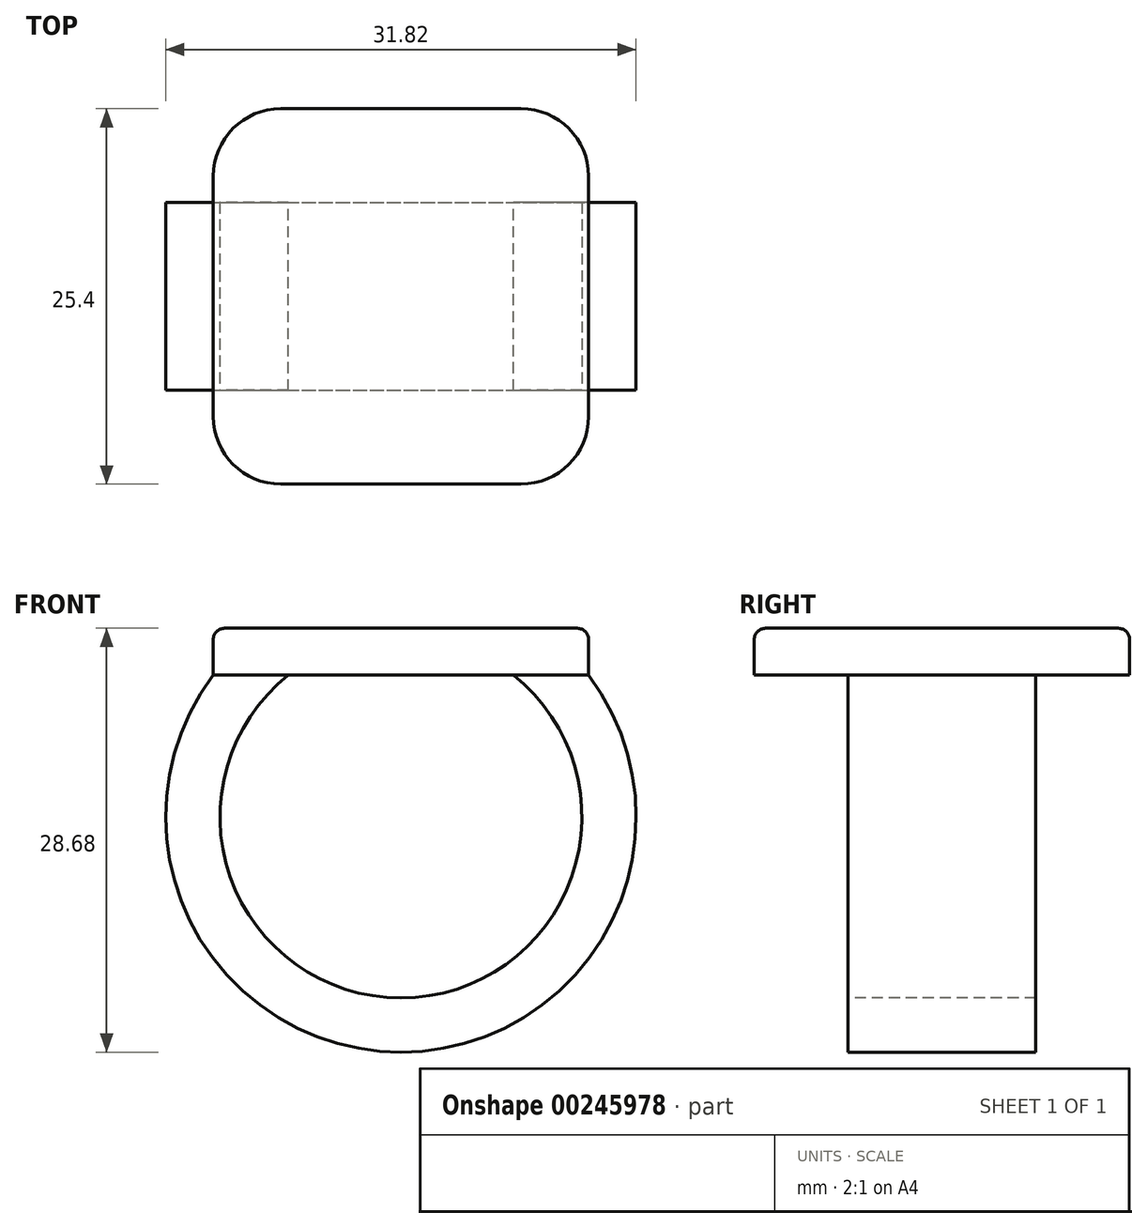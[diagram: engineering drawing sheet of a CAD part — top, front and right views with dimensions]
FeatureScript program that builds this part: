
annotation { "Feature Type Name" : "Feature", "Feature Type Description" : "" }
export const myFeature = defineFeature(function(context is Context, id is Id, definition is map)
    precondition{}
    {
        {
            var Q0;
            Q0=qCreatedBy(makeId("Top.planeOp"),FACE);
            var sketch = newSketch(context, id + "F0", { "sketchPlane" : qUnion([Q0])});
            skLineSegment(sketch, "E0.bottom", {"start": v(12.7, -12.7) * mm, "end": v(-12.7, -12.7) * mm});
            skLineSegment(sketch, "E0.top", {"start": v(12.7, 12.7) * mm, "end": v(-12.7, 12.7) * mm});
            skLineSegment(sketch, "E0.left", {"start": v(12.7, -12.7) * mm, "end": v(12.7, 12.7) * mm});
            skLineSegment(sketch, "E0.right", {"start": v(-12.7, -12.7) * mm, "end": v(-12.7, 12.7) * mm});
            skPoint(sketch, "E0.middle", {"position": v(0, 0) * mm});
            skSolve(sketch);
        }
        {
            var Q0;
            Q0=makeQuery(id+"F0.imprint","IMPRINT",FACE,{"disambiguationData":[TD([[makeQuery(id+"F0.imprint","IMPRINT",EDGE,{"derivedFrom":sQuery(id+"F0.wireOp",EDGE,"E0.bottom")}),-1.0]])]});
            extrude(context, id + "F1", {"entities" : qUnion([Q0]), "depth" : 3.17 * mm});
        }
        {
            var Q0;
            Q0=qCreatedBy(makeId("Front.planeOp"),FACE);
            var sketch = newSketch(context, id + "F2", { "sketchPlane" : qUnion([Q0])});
            skArc(sketch, "E1", {"start": v(-10.16, 0) * mm, "mid": v(0, -23.56) * mm, "end": v(10.16, 0) * mm});
            skSolve(sketch);
        }
        {
            var Q0;
            Q0=makeQuery(id+"F1.opExtrude","CAP_FACE",FACE,{"disambiguationData":[OSD([sQuery(id+"F0.wireOp",EDGE,"E0.bottom"),sQuery(id+"F0.wireOp",EDGE,"E0.top"),sQuery(id+"F0.wireOp",EDGE,"E0.left"),sQuery(id+"F0.wireOp",EDGE,"E0.right")])],"isStart":true});
            var sketch = newSketch(context, id + "F3", { "sketchPlane" : qUnion([Q0])});
            skLineSegment(sketch, "E2.bottom", {"start": v(-12.7, 6.35) * mm, "end": v(-7.62, 6.35) * mm});
            skLineSegment(sketch, "E2.top", {"start": v(-12.7, -6.35) * mm, "end": v(-7.62, -6.35) * mm});
            skLineSegment(sketch, "E2.left", {"start": v(-12.7, 6.35) * mm, "end": v(-12.7, -6.35) * mm});
            skLineSegment(sketch, "E2.right", {"start": v(-7.62, 6.35) * mm, "end": v(-7.62, -6.35) * mm});
            skPoint(sketch, "E2.middle", {"position": v(-10.16, 0) * mm});
            skSolve(sketch);
        }
        {
            var Q0;
            Q0=makeQuery(id+"F3.imprint","IMPRINT",FACE,{"disambiguationData":[TD([[makeQuery(id+"F3.imprint","IMPRINT",EDGE,{"derivedFrom":sQuery(id+"F3.wireOp",EDGE,"E2.bottom")}),-1.0]])]});
            var Q1;
            Q1=sQuery(id+"F2.wireOp",EDGE,"E1");
            sweep(context, id + "F4", {"operationType" : NewBodyOperationType.ADD, "profiles" : qUnion([Q0]), "path" : qUnion([Q1])});
        }
        {
            var Q0;
            Q0=qCreatedBy(makeId("Front.planeOp"),FACE);
            var sketch = newSketch(context, id + "F5", { "sketchPlane" : qUnion([Q0])});
            skLineSegment(sketch, "E3.0", {"start": v(10.16, 0) * mm, "end": v(10.01, -2.54) * mm});
            skLineSegment(sketch, "E4.0", {"start": v(12.7, 0) * mm, "end": v(-12.7, 0) * mm});
            skArc(sketch, "E5", {"start": v(10.01, -2.54) * mm, "mid": v(8.9, -1.18) * mm, "end": v(7.62, 0) * mm});
            skSolve(sketch);
        }
        {
            var Q0;
            {var subQ0=sQuery(id+"F5.wireOp",EDGE,"E3.0");Q0=makeQuery(id+"F5.imprint","IMPRINT",FACE,{"disambiguationData":[TD([[makeQuery(id+"F5.imprint","IMPRINT",EDGE,{"derivedFrom":subQ0}),-1.0]])]});}
            extrude(context, id + "F6", {"entities" : qUnion([Q0]), "operationType" : NewBodyOperationType.ADD, "endBound" : BoundingType.SYMMETRIC, "depth" : 12.7 * mm});
        }
        {
            var Q0;
            Q0=makeQuery(id+"F1.opExtrude","SWEPT_EDGE",EDGE,{"disambiguationData":[OSD([sQuery(id+"F0.wireOp",EDGE,"E0.bottom"),sQuery(id+"F0.wireOp",EDGE,"E0.left")])]});
            var Q1;
            Q1=makeQuery(id+"F1.opExtrude","SWEPT_EDGE",EDGE,{"disambiguationData":[OSD([sQuery(id+"F0.wireOp",EDGE,"E0.top"),sQuery(id+"F0.wireOp",EDGE,"E0.left")])]});
            var Q2;
            Q2=makeQuery(id+"F1.opExtrude","SWEPT_EDGE",EDGE,{"disambiguationData":[OSD([sQuery(id+"F0.wireOp",EDGE,"E0.top"),sQuery(id+"F0.wireOp",EDGE,"E0.right")])]});
            var Q3;
            Q3=makeQuery(id+"F1.opExtrude","SWEPT_EDGE",EDGE,{"disambiguationData":[OSD([sQuery(id+"F0.wireOp",EDGE,"E0.bottom"),sQuery(id+"F0.wireOp",EDGE,"E0.right")])]});
            fillet(context, id + "F7", {"entities" : qUnion([Q0, Q1, Q2, Q3]), "radius" : 4.57 * mm, "tangentPropagation" : true, "allowEdgeOverflow" : false});
        }
        {
            var Q0;
            Q0=makeQuery(id+"F1.opExtrude","CAP_FACE",FACE,{"disambiguationData":[OSD([sQuery(id+"F0.wireOp",EDGE,"E0.bottom"),sQuery(id+"F0.wireOp",EDGE,"E0.top"),sQuery(id+"F0.wireOp",EDGE,"E0.left"),sQuery(id+"F0.wireOp",EDGE,"E0.right")])],"isStart":false});
            fillet(context, id + "F8", {"entities" : qUnion([Q0]), "radius" : 0.76 * mm, "tangentPropagation" : true, "allowEdgeOverflow" : false});
        }
    });
